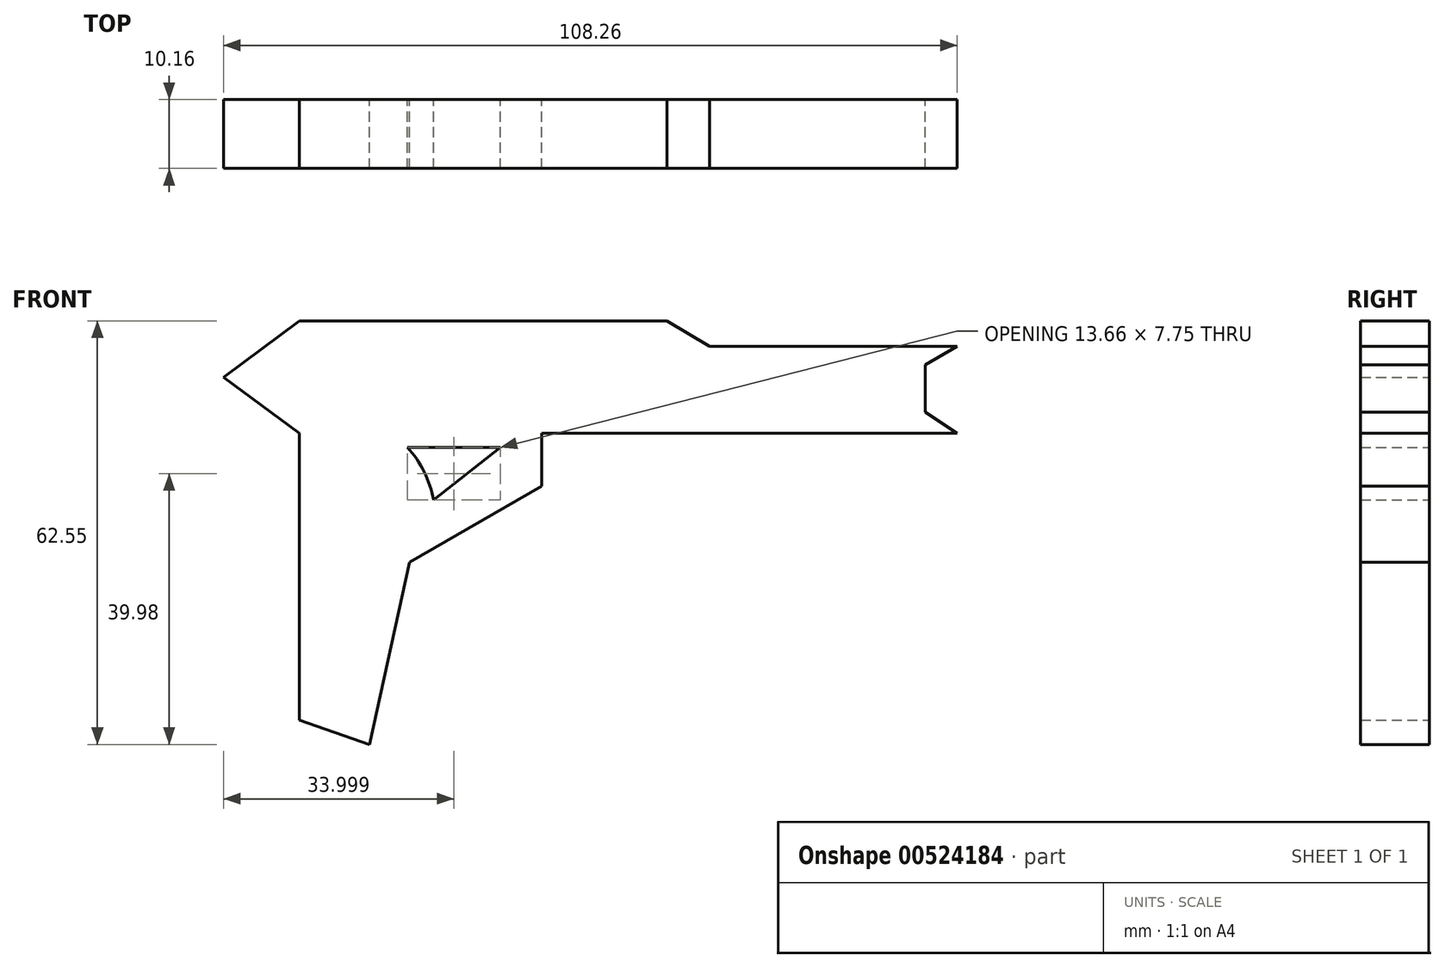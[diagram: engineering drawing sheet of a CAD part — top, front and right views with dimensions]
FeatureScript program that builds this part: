
annotation { "Feature Type Name" : "Feature", "Feature Type Description" : "" }
export const myFeature = defineFeature(function(context is Context, id is Id, definition is map)
    precondition{}
    {
        {
            var Q0;
            Q0=qCreatedBy(makeId("Front.planeOp"),FACE);
            var sketch = newSketch(context, id + "F0", { "sketchPlane" : qUnion([Q0])});
            skLineSegment(sketch, "E0", {"start": v(0, 0) * mm, "end": v(36.52, 0) * mm});
            skLineSegment(sketch, "E1", {"start": v(36.52, 0) * mm, "end": v(31.77, 3.1) * mm});
            skLineSegment(sketch, "E2", {"start": v(31.77, 3.1) * mm, "end": v(31.77, 10.14) * mm});
            skLineSegment(sketch, "E3", {"start": v(31.77, 10.14) * mm, "end": v(36.52, 12.87) * mm});
            skLineSegment(sketch, "E4", {"start": v(36.52, 12.87) * mm, "end": v(0, 12.87) * mm});
            skLineSegment(sketch, "E5", {"start": v(0, 12.87) * mm, "end": v(-6.33, 16.6) * mm});
            skLineSegment(sketch, "E6", {"start": v(-6.33, 16.6) * mm, "end": v(-60.53, 16.6) * mm});
            skLineSegment(sketch, "E7", {"start": v(-60.53, 16.6) * mm, "end": v(-71.74, 8.27) * mm});
            skLineSegment(sketch, "E8", {"start": v(-71.74, 8.27) * mm, "end": v(-60.53, 0) * mm});
            skLineSegment(sketch, "E9", {"start": v(-60.53, 0) * mm, "end": v(-60.53, -42.34) * mm});
            skLineSegment(sketch, "E10", {"start": v(-60.53, -42.34) * mm, "end": v(-50.18, -45.94) * mm});
            skLineSegment(sketch, "E11", {"start": v(-50.18, -45.94) * mm, "end": v(-44.28, -19.05) * mm});
            skLineSegment(sketch, "E12", {"start": v(-44.28, -19.05) * mm, "end": v(-24.76, -7.81) * mm});
            skLineSegment(sketch, "E13", {"start": v(-24.76, -7.81) * mm, "end": v(-24.76, 0) * mm});
            skLineSegment(sketch, "E14", {"start": v(-24.76, 0) * mm, "end": v(36.52, 0) * mm});
            skLineSegment(sketch, "E15", {"start": v(-44.57, -12.87) * mm, "end": v(-44.57, -2.08) * mm});
            skLineSegment(sketch, "E16", {"start": v(-44.57, -2.08) * mm, "end": v(-30.91, -2.08) * mm});
            skLineSegment(sketch, "E17", {"start": v(-30.91, -2.08) * mm, "end": v(-44.57, -12.87) * mm});
            skArc(sketch, "E18", {"start": v(-40.73, -9.84) * mm, "mid": v(-42.13, -5.7) * mm, "end": v(-44.57, -2.08) * mm});
            skSolve(sketch);
        }
        {
            var Q0;
            {var subQ0=sQuery(id+"F0.wireOp",EDGE,"E1");Q0=makeQuery(id+"F0.imprint","IMPRINT",FACE,{"disambiguationData":[TD([[makeQuery(id+"F0.imprint","IMPRINT",EDGE,{"derivedFrom":subQ0}),1.0]])]});}
            var Q1;
            {var subQ0=sQuery(id+"F0.wireOp",EDGE,"E15");Q1=makeQuery(id+"F0.imprint","IMPRINT",FACE,{"disambiguationData":[TD([[makeQuery(id+"F0.imprint","IMPRINT",EDGE,{"derivedFrom":subQ0}),-1.0]])]});}
            extrude(context, id + "F1", {"entities" : qUnion([Q0, Q1]), "depth" : 10.16 * mm, "offsetDistance" : 25.4 * mm});
        }
    });
